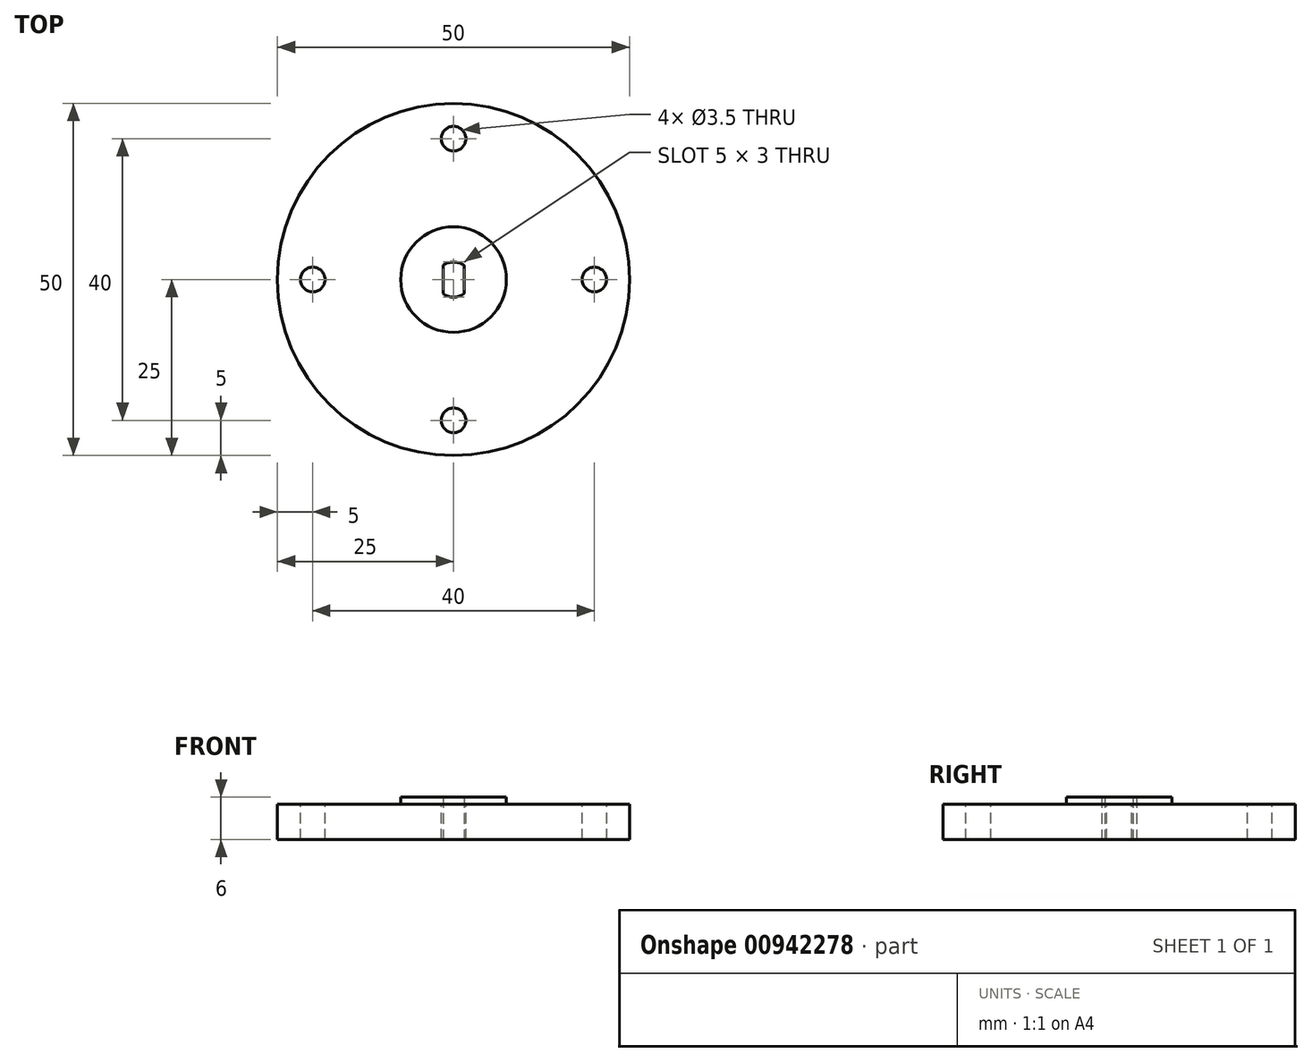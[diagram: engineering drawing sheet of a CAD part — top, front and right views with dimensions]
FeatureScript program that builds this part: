
annotation { "Feature Type Name" : "Feature", "Feature Type Description" : "" }
export const myFeature = defineFeature(function(context is Context, id is Id, definition is map)
    precondition{}
    {
        {
            var Q0;
            Q0=qCreatedBy(makeId("Top.planeOp"),FACE);
            var sketch = newSketch(context, id + "F0", { "sketchPlane" : qUnion([Q0])});
            skArc(sketch, "E0", {"start": v(-1.5, -2) * mm, "mid": v(0, -2.5) * mm, "end": v(1.5, -2) * mm});
            skLineSegment(sketch, "E1.left", {"start": v(1.5, 2) * mm, "end": v(1.5, -2) * mm});
            skLineSegment(sketch, "E1.right", {"start": v(-1.5, 2) * mm, "end": v(-1.5, -2) * mm});
            skPoint(sketch, "E2.orphan", {"position": v(1.5, 3.22) * mm});
            skPoint(sketch, "E3.orphan", {"position": v(-1.5, 3.22) * mm});
            skArc(sketch, "E4.trimOffspring", {"start": v(1.5, 2) * mm, "mid": v(0, 2.5) * mm, "end": v(-1.5, 2) * mm});
            skPoint(sketch, "E5.orphan", {"position": v(1.5, -3.22) * mm});
            skPoint(sketch, "E6.orphan", {"position": v(-1.5, -3.22) * mm});
            skCircle(sketch, "E7", {"center": v(0, 0) * mm, "radius": 25 * mm});
            skCircle(sketch, "E8", {"center": v(0, 0) * mm, "radius": 7.5 * mm});
            skSolve(sketch);
        }
        {
            var Q0;
            Q0=makeQuery(id+"F0.imprint","IMPRINT",FACE,{"disambiguationData":[TD([[makeQuery(id+"F0.imprint","IMPRINT",EDGE,{"derivedFrom":sQuery(id+"F0.wireOp",EDGE,"E0")}),-1.0]])]});
            var Q1;
            Q1=makeQuery(id+"F0.imprint","IMPRINT",FACE,{"disambiguationData":[TD([[makeQuery(id+"F0.imprint","IMPRINT",EDGE,{"derivedFrom":sQuery(id+"F0.wireOp",EDGE,"E7")}),1.0]])]});
            extrude(context, id + "F1", {"entities" : qUnion([Q0, Q1]), "depth" : 5 * mm, "offsetDistance" : 25 * mm});
        }
        {
            var Q0;
            Q0=makeQuery(id+"F0.imprint","IMPRINT",FACE,{"disambiguationData":[TD([[makeQuery(id+"F0.imprint","IMPRINT",EDGE,{"derivedFrom":sQuery(id+"F0.wireOp",EDGE,"E0")}),-1.0]])]});
            extrude(context, id + "F2", {"entities" : qUnion([Q0]), "operationType" : NewBodyOperationType.ADD, "depth" : 6 * mm, "offsetDistance" : 25 * mm});
        }
        {
            var Q0;
            Q0=makeQuery(id+"F1.opExtrude","CAP_FACE",FACE,{"disambiguationData":[OSD([sQuery(id+"F0.wireOp",EDGE,"E0"),sQuery(id+"F0.wireOp",EDGE,"E1.left"),sQuery(id+"F0.wireOp",EDGE,"E1.right"),sQuery(id+"F0.wireOp",EDGE,"E4.trimOffspring"),sQuery(id+"F0.wireOp",EDGE,"E7")])],"isStart":false});
            var sketch = newSketch(context, id + "F3", { "sketchPlane" : qUnion([Q0])});
            skCircle(sketch, "E9", {"center": v(0, 20) * mm, "radius": 1.75 * mm});
            skLineSegment(sketch, "E10", {"start": v(0, 0) * mm, "end": v(0, 20) * mm});
            skCircle(sketch, "E11.1.0", {"center": v(-20, 0) * mm, "radius": 1.75 * mm});
            skCircle(sketch, "E11.2.0", {"center": v(0, -20) * mm, "radius": 1.75 * mm});
            skPoint(sketch, "E11.center", {"position": v(0, 0) * mm});
            skCircle(sketch, "E12.1.3.0", {"center": v(20, 0) * mm, "radius": 1.75 * mm});
            skSolve(sketch);
        }
        {
            var Q0;
            Q0=makeQuery(id+"F3.imprint","IMPRINT",FACE,{"disambiguationData":[TD([[makeQuery(id+"F3.imprint","IMPRINT",EDGE,{"derivedFrom":sQuery(id+"F3.wireOp",EDGE,"E9")}),1.0]])]});
            var Q1;
            Q1=makeQuery(id+"F3.imprint","IMPRINT",FACE,{"disambiguationData":[TD([[makeQuery(id+"F3.imprint","IMPRINT",EDGE,{"derivedFrom":sQuery(id+"F3.wireOp",EDGE,"E12.1.3.0")}),1.0]])]});
            var Q2;
            Q2=makeQuery(id+"F3.imprint","IMPRINT",FACE,{"disambiguationData":[TD([[makeQuery(id+"F3.imprint","IMPRINT",EDGE,{"derivedFrom":sQuery(id+"F3.wireOp",EDGE,"E11.2.0")}),1.0]])]});
            var Q3;
            Q3=makeQuery(id+"F3.imprint","IMPRINT",FACE,{"disambiguationData":[TD([[makeQuery(id+"F3.imprint","IMPRINT",EDGE,{"derivedFrom":sQuery(id+"F3.wireOp",EDGE,"E11.1.0")}),1.0]])]});
            extrude(context, id + "F4", {"entities" : qUnion([Q0, Q1, Q2, Q3]), "operationType" : NewBodyOperationType.REMOVE, "oppositeDirection" : true, "depth" : 5 * mm, "offsetDistance" : 25 * mm});
        }
    });
